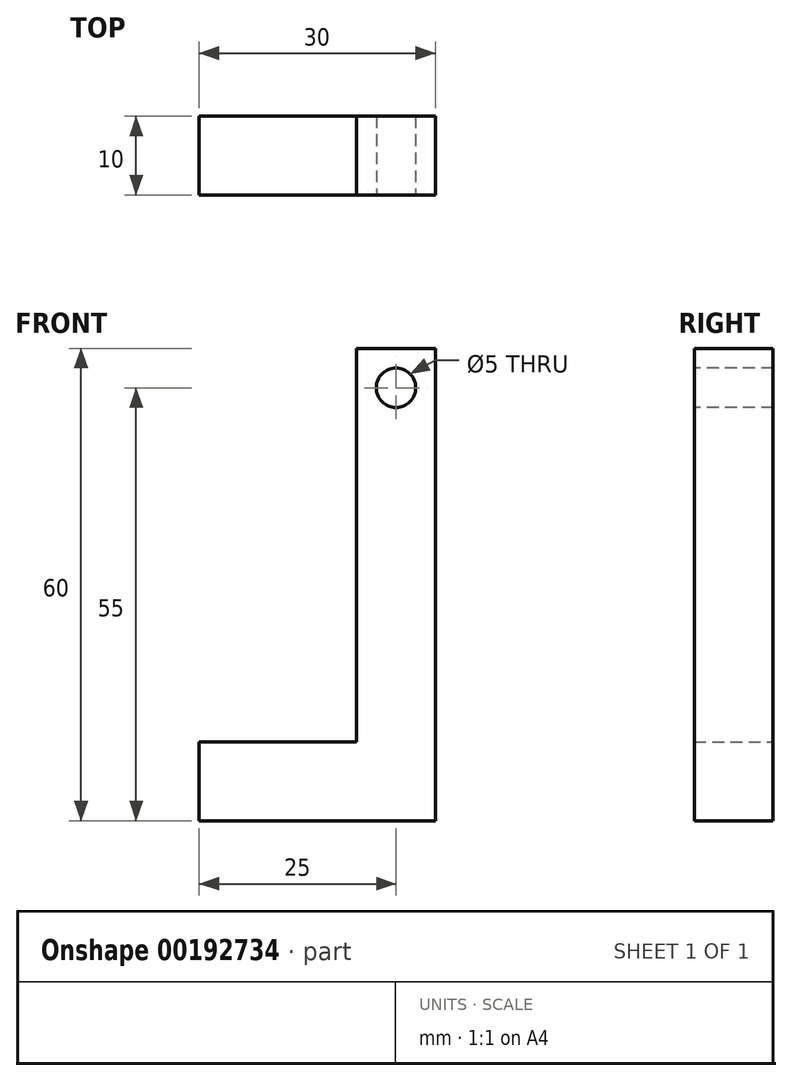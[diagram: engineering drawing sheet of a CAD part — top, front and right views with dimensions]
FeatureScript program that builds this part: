
annotation { "Feature Type Name" : "Feature", "Feature Type Description" : "" }
export const myFeature = defineFeature(function(context is Context, id is Id, definition is map)
    precondition{}
    {
        {
            var Q0;
            Q0=qCreatedBy(makeId("Front.planeOp"),FACE);
            var sketch = newSketch(context, id + "F0", { "sketchPlane" : qUnion([Q0])});
            skLineSegment(sketch, "E0.bottom", {"start": v(5, 25) * mm, "end": v(-5, 25) * mm});
            skLineSegment(sketch, "E0.top", {"start": v(5, -25) * mm, "end": v(-5, -25) * mm});
            skLineSegment(sketch, "E0.left", {"start": v(5, 25) * mm, "end": v(5, -25) * mm});
            skLineSegment(sketch, "E0.right", {"start": v(-5, 25) * mm, "end": v(-5, -25) * mm});
            skPoint(sketch, "E0.middle", {"position": v(0, 0) * mm});
            skLineSegment(sketch, "E1.bottom", {"start": v(5, -25) * mm, "end": v(-25, -25) * mm});
            skLineSegment(sketch, "E1.top", {"start": v(5, -35) * mm, "end": v(-25, -35) * mm});
            skLineSegment(sketch, "E1.left", {"start": v(5, -25) * mm, "end": v(5, -35) * mm});
            skLineSegment(sketch, "E1.right", {"start": v(-25, -25) * mm, "end": v(-25, -35) * mm});
            skSolve(sketch);
        }
        {
            var Q0;
            Q0 = qSketchRegion(id + "F0", true);
            extrude(context, id + "F1", {"entities" : qUnion([Q0]), "depth" : 10 * mm});
        }
        {
            var Q0;
            Q0=makeQuery(id+"F1.opExtrude","CAP_FACE",FACE,{"disambiguationData":[OSD([sQuery(id+"F0.wireOp",EDGE,"E0.bottom"),sQuery(id+"F0.wireOp",EDGE,"E0.left"),sQuery(id+"F0.wireOp",EDGE,"E0.right"),sQuery(id+"F0.wireOp",EDGE,"E1.bottom"),sQuery(id+"F0.wireOp",EDGE,"E1.top"),sQuery(id+"F0.wireOp",EDGE,"E1.left"),sQuery(id+"F0.wireOp",EDGE,"E1.right")])],"isStart":false});
            var sketch = newSketch(context, id + "F2", { "sketchPlane" : qUnion([Q0])});
            skCircle(sketch, "E2", {"center": v(0, 20) * mm, "radius": 2.5 * mm});
            skSolve(sketch);
        }
        {
            var Q0;
            Q0 = qSketchRegion(id + "F2", true);
            extrude(context, id + "F3", {"entities" : qUnion([Q0]), "operationType" : NewBodyOperationType.REMOVE, "endBound" : BoundingType.UP_TO_NEXT, "oppositeDirection" : true, "depth" : 25 * mm});
        }
    });
